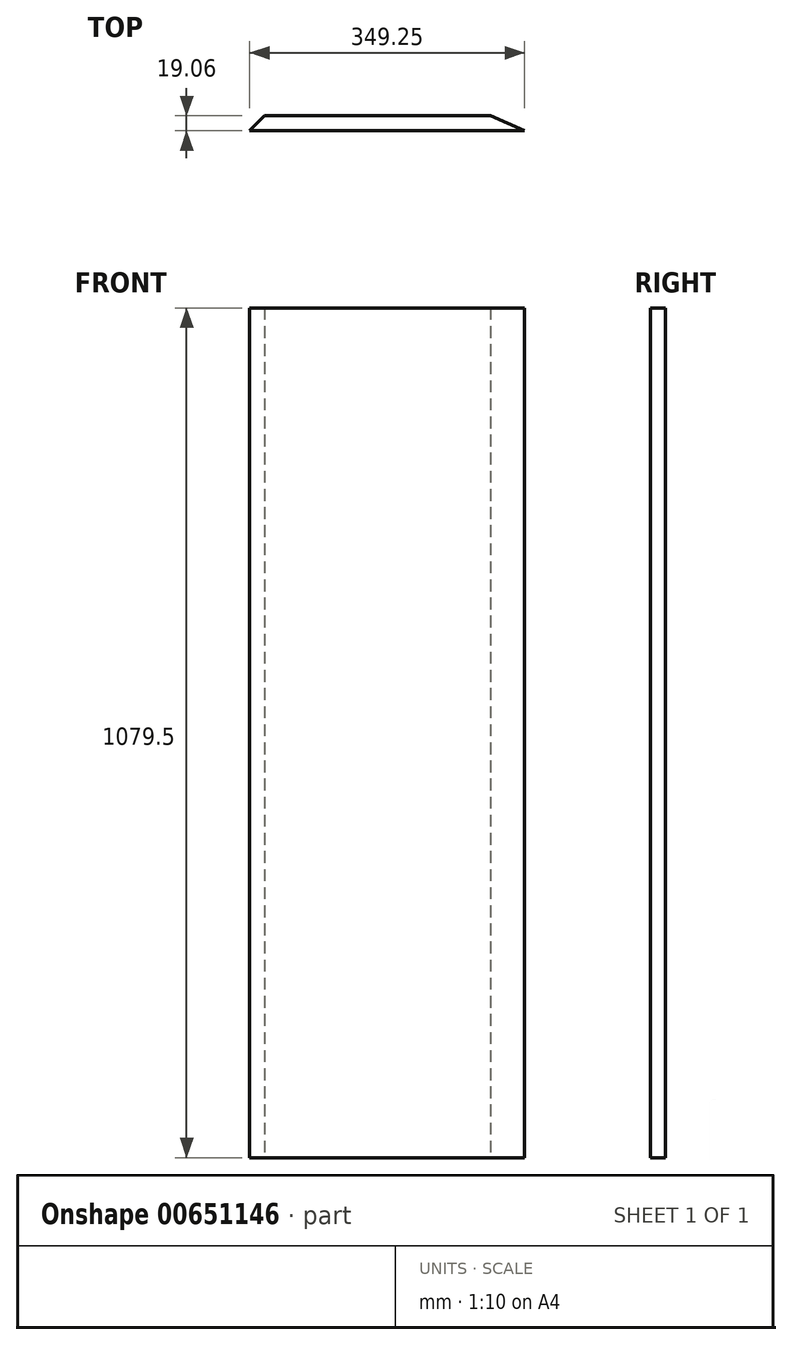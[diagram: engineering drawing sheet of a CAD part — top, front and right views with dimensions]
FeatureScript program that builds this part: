
annotation { "Feature Type Name" : "Feature", "Feature Type Description" : "" }
export const myFeature = defineFeature(function(context is Context, id is Id, definition is map)
    precondition{}
    {
        {
            var Q0;
            Q0=qCreatedBy(makeId("Top.planeOp"),FACE);
            var sketch = newSketch(context, id + "F0", { "sketchPlane" : qUnion([Q0])});
            skLineSegment(sketch, "E0", {"start": v(180.69, -9.53) * mm, "end": v(-168.56, -9.53) * mm});
            skLineSegment(sketch, "E1.trimOffspring", {"start": v(137.38, 9.52) * mm, "end": v(-149.51, 9.52) * mm});
            skLineSegment(sketch, "E2", {"start": v(137.38, 9.53) * mm, "end": v(180.69, -9.53) * mm});
            skLineSegment(sketch, "E3", {"start": v(-149.51, 9.53) * mm, "end": v(-168.56, -9.52) * mm});
            skSolve(sketch);
        }
        {
            var Q0;
            Q0=makeQuery(id+"F0.imprint","IMPRINT",FACE,{"disambiguationData":[TD([[makeQuery(id+"F0.imprint","IMPRINT",EDGE,{"derivedFrom":sQuery(id+"F0.wireOp",EDGE,"E0")}),-1.0]])]});
            extrude(context, id + "F1", {"entities" : qUnion([Q0]), "depth" : 1079.5 * mm, "offsetDistance" : 25.4 * mm});
        }
    });
